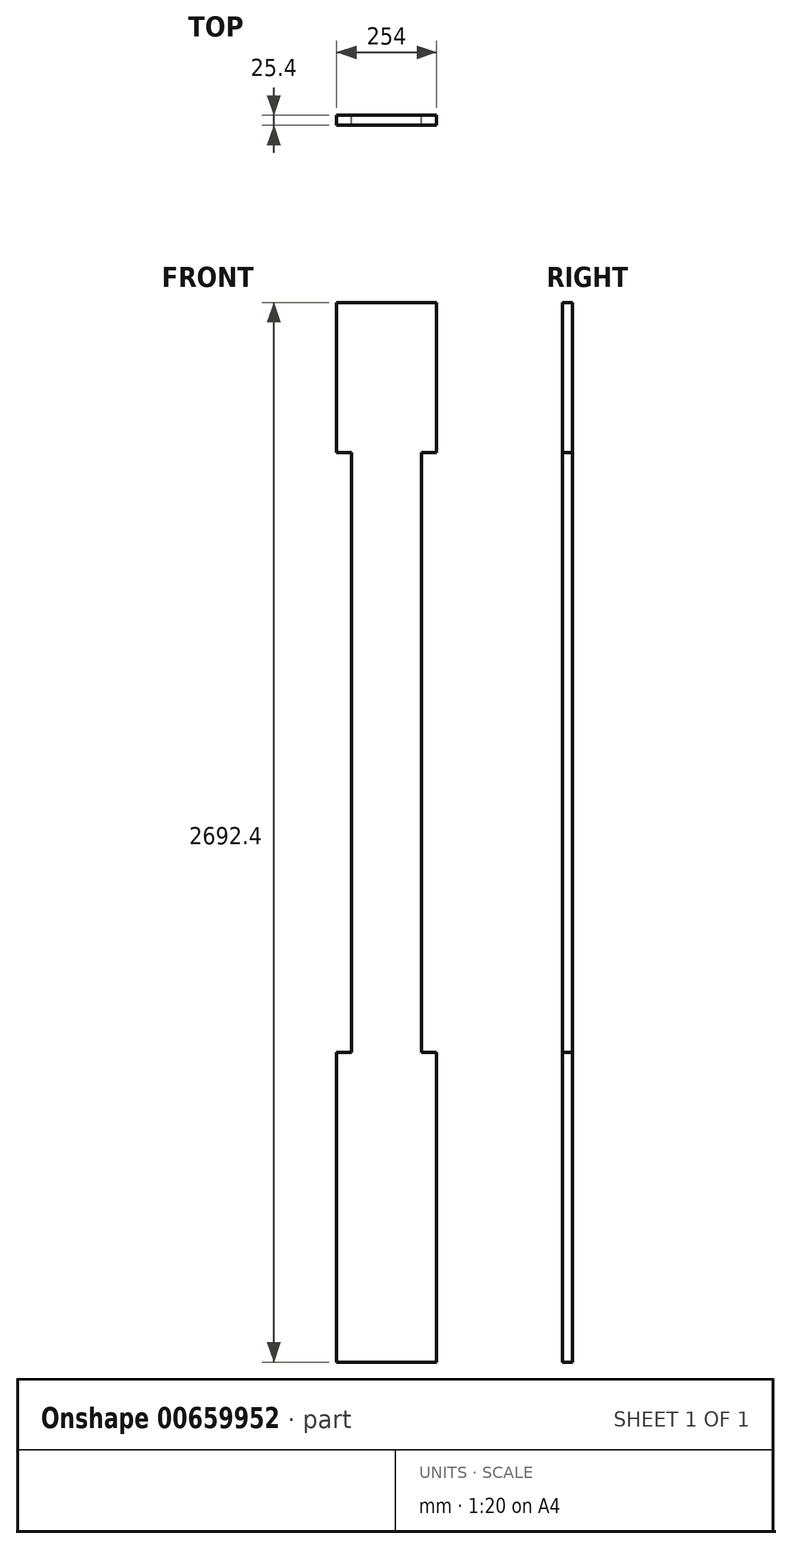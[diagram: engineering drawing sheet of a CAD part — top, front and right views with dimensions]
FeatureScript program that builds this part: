
annotation { "Feature Type Name" : "Feature", "Feature Type Description" : "" }
export const myFeature = defineFeature(function(context is Context, id is Id, definition is map)
    precondition{}
    {
        {
            var Q0;
            Q0=qCreatedBy(makeId("Front.planeOp"),FACE);
            var sketch = newSketch(context, id + "F0", { "sketchPlane" : qUnion([Q0])});
            skLineSegment(sketch, "E0.bottom", {"start": v(127, 0) * mm, "end": v(-127, 0) * mm});
            skLineSegment(sketch, "E0.top", {"start": v(127, 787.4) * mm, "end": v(88.9, 787.4) * mm});
            skLineSegment(sketch, "E0.left", {"start": v(127, 0) * mm, "end": v(127, 787.4) * mm});
            skLineSegment(sketch, "E0.right", {"start": v(-127, 0) * mm, "end": v(-127, 787.4) * mm});
            skPoint(sketch, "E0.middle", {"position": v(0, 393.7) * mm});
            skLineSegment(sketch, "E1.left", {"start": v(88.9, 787.4) * mm, "end": v(88.9, 2311.4) * mm});
            skLineSegment(sketch, "E1.right", {"start": v(-88.9, 787.4) * mm, "end": v(-88.9, 2311.4) * mm});
            skPoint(sketch, "E1.middle", {"position": v(0, 1549.4) * mm});
            skLineSegment(sketch, "E2.bottom", {"start": v(127, 2311.4) * mm, "end": v(88.9, 2311.4) * mm});
            skLineSegment(sketch, "E2.top", {"start": v(127, 2692.4) * mm, "end": v(-127, 2692.4) * mm});
            skLineSegment(sketch, "E2.left", {"start": v(127, 2311.4) * mm, "end": v(127, 2692.4) * mm});
            skLineSegment(sketch, "E2.right", {"start": v(-127, 2311.4) * mm, "end": v(-127, 2692.4) * mm});
            skPoint(sketch, "E2.middle", {"position": v(0, 2501.9) * mm});
            skLineSegment(sketch, "E3.trimOffspring", {"start": v(-88.9, 2311.4) * mm, "end": v(-127, 2311.4) * mm});
            skLineSegment(sketch, "E4.trimOffspring", {"start": v(-88.9, 787.4) * mm, "end": v(-127, 787.4) * mm});
            skSolve(sketch);
        }
        {
            var Q0;
            Q0 = qSketchRegion(id + "F0", true);
            extrude(context, id + "F1", {"entities" : qUnion([Q0]), "depth" : 25.4 * mm, "offsetDistance" : 25.4 * mm});
        }
    });
